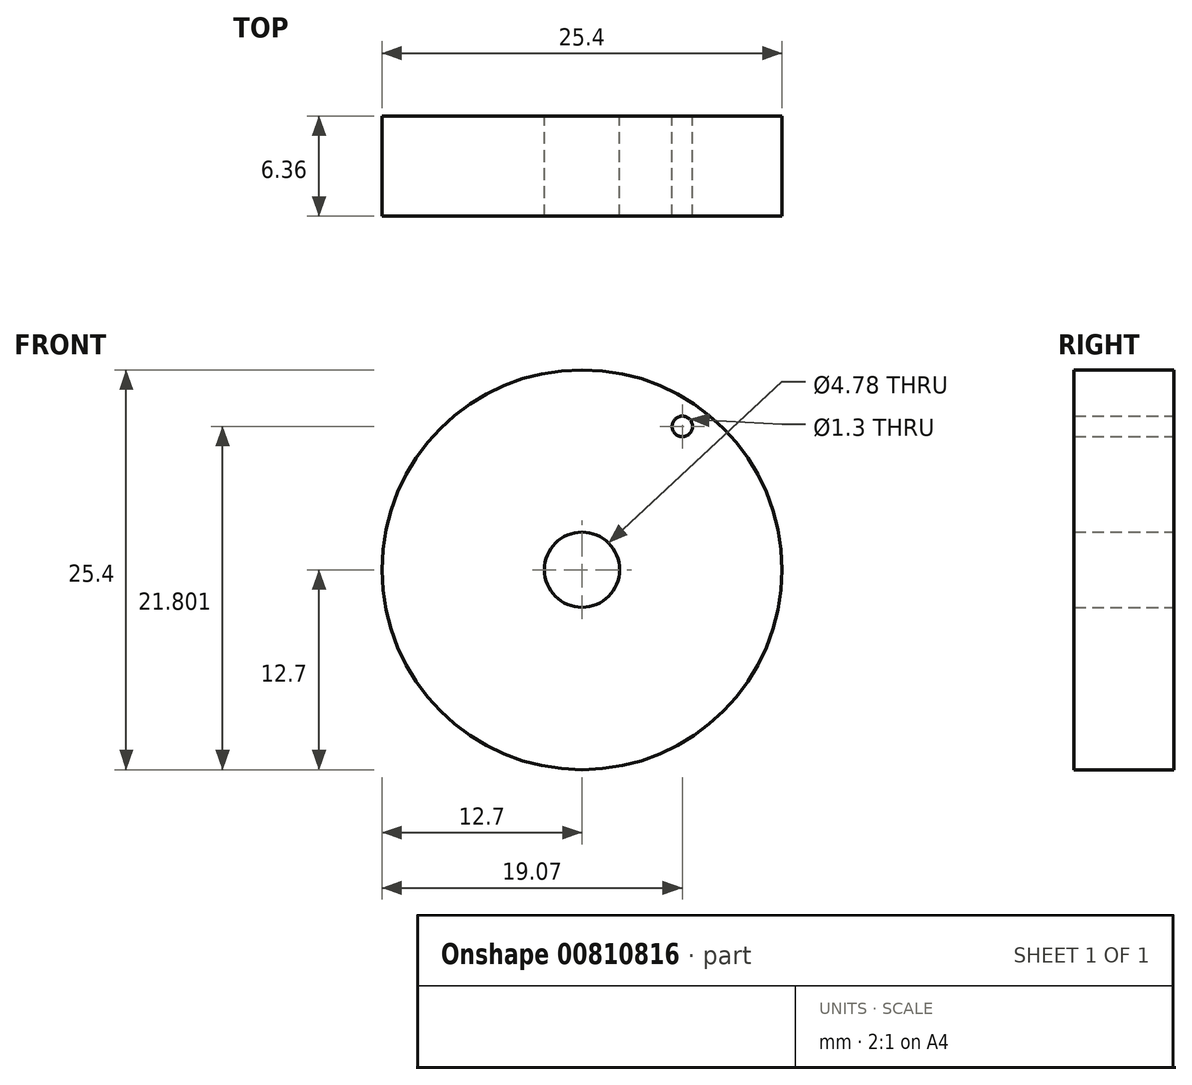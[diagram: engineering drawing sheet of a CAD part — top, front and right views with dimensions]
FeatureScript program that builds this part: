
annotation { "Feature Type Name" : "Feature", "Feature Type Description" : "" }
export const myFeature = defineFeature(function(context is Context, id is Id, definition is map)
    precondition{}
    {
        {
            var Q0;
            Q0=qCreatedBy(makeId("Front.planeOp"),FACE);
            var sketch = newSketch(context, id + "F0", { "sketchPlane" : qUnion([Q0])});
            skCircle(sketch, "E0", {"center": v(0, 0) * mm, "radius": 12.7 * mm});
            skCircle(sketch, "E1", {"center": v(0, 0) * mm, "radius": 2.39 * mm});
            skCircle(sketch, "E2", {"center": v(6.37, 9.1) * mm, "radius": 0.65 * mm});
            skSolve(sketch);
        }
        {
            var Q0;
            Q0=makeQuery(id+"F0.imprint","IMPRINT",FACE,{"disambiguationData":[TD([[makeQuery(id+"F0.imprint","IMPRINT",EDGE,{"derivedFrom":sQuery(id+"F0.wireOp",EDGE,"E0")}),1.0]])]});
            extrude(context, id + "F1", {"entities" : qUnion([Q0]), "endBound" : BoundingType.SYMMETRIC, "depth" : 6.35 * mm, "offsetDistance" : 25.4 * mm});
        }
    });
